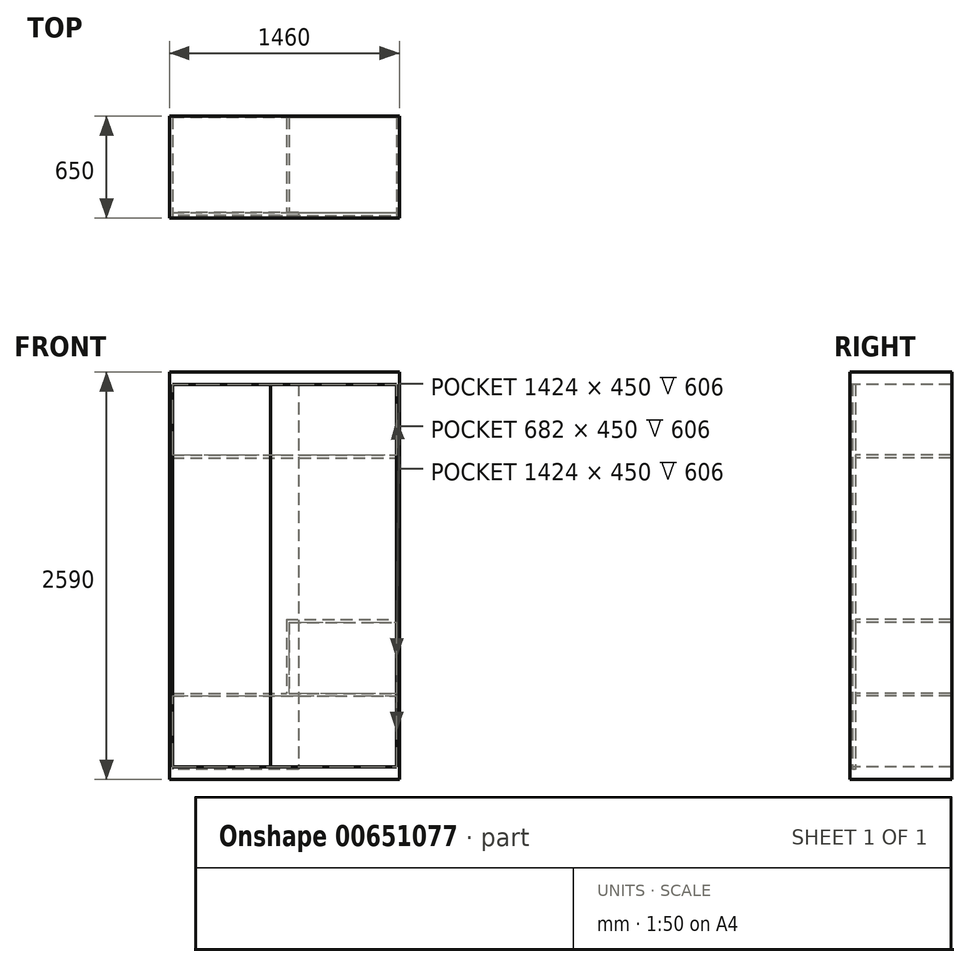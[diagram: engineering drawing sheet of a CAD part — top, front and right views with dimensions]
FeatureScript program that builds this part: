
annotation { "Feature Type Name" : "Feature", "Feature Type Description" : "" }
export const myFeature = defineFeature(function(context is Context, id is Id, definition is map)
    precondition{}
    {
        {
            var Q0;
            Q0=qCreatedBy(makeId("Top.planeOp"),FACE);
            var sketch = newSketch(context, id + "F0", { "sketchPlane" : qUnion([Q0])});
            skLineSegment(sketch, "E0.bottom", {"start": v(0, 0) * mm, "end": v(-1460, 0) * mm});
            skLineSegment(sketch, "E0.top", {"start": v(0, 650) * mm, "end": v(-1460, 650) * mm});
            skLineSegment(sketch, "E0.left", {"start": v(0, 0) * mm, "end": v(0, 650) * mm});
            skLineSegment(sketch, "E0.right", {"start": v(-1460, 0) * mm, "end": v(-1460, 650) * mm});
            skPoint(sketch, "E1.oppositeSnap0", {"position": v(-1460, 325) * mm});
            skLineSegment(sketch, "E1.bottom", {"start": v(-1460, 0) * mm, "end": v(-2355, 0) * mm});
            skLineSegment(sketch, "E1.left", {"start": v(-1460, 0) * mm, "end": v(-1460, 325) * mm});
            skLineSegment(sketch, "E1.right", {"start": v(-2355, 0) * mm, "end": v(-2355, 325) * mm});
            skLineSegment(sketch, "E2.bottom", {"start": v(-1460, 430) * mm, "end": v(-2355, 430) * mm});
            skLineSegment(sketch, "E2.left", {"start": v(-1460, 430) * mm, "end": v(-1460, 325) * mm});
            skLineSegment(sketch, "E2.right", {"start": v(-2355, 430) * mm, "end": v(-2355, 325) * mm});
            skSolve(sketch);
        }
        {
            var Q0;
            Q0=makeQuery(id+"F0.imprint","IMPRINT",FACE,{"disambiguationData":[TD([[makeQuery(id+"F0.imprint","IMPRINT",EDGE,{"derivedFrom":sQuery(id+"F0.wireOp",EDGE,"E0.bottom")}),-1.0]])]});
            extrude(context, id + "F1", {"entities" : qUnion([Q0]), "depth" : 2590 * mm, "offsetDistance" : 25 * mm});
        }
        {
            var Q0;
            Q0=makeQuery(id+"F1.opExtrude","SWEPT_FACE",FACE,{"disambiguationData":[OSD([sQuery(id+"F0.wireOp",EDGE,"E0.bottom")])]});
            var sketch = newSketch(context, id + "F2", { "sketchPlane" : qUnion([Q0])});
            skLineSegment(sketch, "E3.bottom", {"start": v(-1442, 2510) * mm, "end": v(-18, 2510) * mm});
            skLineSegment(sketch, "E3.top", {"start": v(-1442, 80) * mm, "end": v(-18, 80) * mm});
            skLineSegment(sketch, "E3.left", {"start": v(-1442, 2510) * mm, "end": v(-1442, 80) * mm});
            skLineSegment(sketch, "E3.right", {"start": v(-18, 2510) * mm, "end": v(-18, 80) * mm});
            skSolve(sketch);
        }
        {
            var Q0;
            Q0=qSketchRegion(id+"F2",true);
            extrude(context, id + "F3", {"entities" : qUnion([Q0]), "operationType" : NewBodyOperationType.REMOVE, "oppositeDirection" : true, "depth" : 36 * mm, "offsetDistance" : 25 * mm});
        }
        {
            var Q0;
            Q0=makeQuery(id+"F3.boolean.opBoolean","COPY",FACE,{"derivedFrom":makeQuery(id+"F3.opExtrude","CAP_FACE",FACE,{"disambiguationData":[OSD([sQuery(id+"F2.wireOp",EDGE,"E3.bottom"),sQuery(id+"F2.wireOp",EDGE,"E3.top"),sQuery(id+"F2.wireOp",EDGE,"E3.left"),sQuery(id+"F2.wireOp",EDGE,"E3.right")])],"isStart":false})});
            var sketch = newSketch(context, id + "F4", { "sketchPlane" : qUnion([Q0])});
            skLineSegment(sketch, "E4.bottom", {"start": v(-1442, 2510) * mm, "end": v(-18, 2510) * mm});
            skLineSegment(sketch, "E4.top", {"start": v(-1442, 2060) * mm, "end": v(-18, 2060) * mm});
            skLineSegment(sketch, "E4.left", {"start": v(-1442, 2510) * mm, "end": v(-1442, 2060) * mm});
            skLineSegment(sketch, "E4.right", {"start": v(-18, 2510) * mm, "end": v(-18, 2060) * mm});
            skLineSegment(sketch, "E5.bottom", {"start": v(-1442, 2042) * mm, "end": v(-18, 2042) * mm});
            skLineSegment(sketch, "E5.top", {"start": v(-718, 1016) * mm, "end": v(-18, 1016) * mm});
            skLineSegment(sketch, "E5.right", {"start": v(-18, 2042) * mm, "end": v(-18, 1016) * mm});
            skLineSegment(sketch, "E6.top", {"start": v(-1442, 548) * mm, "end": v(-718, 548) * mm});
            skLineSegment(sketch, "E6.right", {"start": v(-718, 1016) * mm, "end": v(-718, 548) * mm});
            skLineSegment(sketch, "E7.left", {"start": v(-1442, 530) * mm, "end": v(-1442, 104.26) * mm});
            skLineSegment(sketch, "E8.bottom", {"start": v(-700, 998) * mm, "end": v(-18, 998) * mm});
            skLineSegment(sketch, "E8.top", {"start": v(-700, 548) * mm, "end": v(-18, 548) * mm});
            skLineSegment(sketch, "E8.left", {"start": v(-700, 998) * mm, "end": v(-700, 548) * mm});
            skLineSegment(sketch, "E8.right", {"start": v(-18, 998) * mm, "end": v(-18, 548) * mm});
            skLineSegment(sketch, "E9.bottom", {"start": v(-1442, 530) * mm, "end": v(-18, 530) * mm});
            skLineSegment(sketch, "E9.right", {"start": v(-18, 530) * mm, "end": v(-18, 80) * mm});
            skSolve(sketch);
        }
        {
            var Q0;
            Q0=makeQuery(id+"F4.imprint","IMPRINT",FACE,{"disambiguationData":[TD([[makeQuery(id+"F4.imprint","IMPRINT",EDGE,{"derivedFrom":sQuery(id+"F4.wireOp",EDGE,"E4.bottom")}),-1.0]])]});
            var Q1;
            Q1=makeQuery(id+"F4.imprint","IMPRINT",FACE,{"disambiguationData":[TD([[makeQuery(id+"F4.imprint","IMPRINT",EDGE,{"derivedFrom":sQuery(id+"F4.wireOp",EDGE,"E8.bottom")}),-1.0]])]});
            var Q2;
            {var subQ1=sQuery(id+"F4.wireOp",EDGE,"E5.bottom");Q2=makeQuery(id+"F4.imprint","IMPRINT",FACE,{"disambiguationData":[TD([[makeQuery(id+"F4.imprint","IMPRINT",EDGE,{"derivedFrom":subQ1}),-1.0]])]});}
            var Q3;
            Q3=makeQuery(id+"F4.imprint","IMPRINT",FACE,{"disambiguationData":[TD([[makeQuery(id+"F4.imprint","IMPRINT",EDGE,{"derivedFrom":sQuery(id+"F4.wireOp",EDGE,"E9.bottom")}),-1.0]])]});
            extrude(context, id + "F5", {"entities" : qUnion([Q0, Q1, Q2, Q3]), "operationType" : NewBodyOperationType.REMOVE, "oppositeDirection" : true, "depth" : 606 * mm, "offsetDistance" : 25 * mm});
        }
        {
            var Q0;
            Q0=makeQuery(id+"F5.boolean.opBoolean","MERGE",FACE,{"derivedFrom":[makeQuery(id+"F3.boolean.opBoolean","COPY",FACE,{"derivedFrom":makeQuery(id+"F3.opExtrude","SWEPT_FACE",FACE,{"disambiguationData":[OSD([sQuery(id+"F2.wireOp",EDGE,"E3.right")])]})}),makeQuery(id+"F5.opExtrude","SWEPT_FACE",FACE,{"disambiguationData":[OSD([sQuery(id+"F4.wireOp",EDGE,"E4.right")])]}),makeQuery(id+"F5.opExtrude","SWEPT_FACE",FACE,{"disambiguationData":[OSD([sQuery(id+"F4.wireOp",EDGE,"E5.right")])]}),makeQuery(id+"F5.opExtrude","SWEPT_FACE",FACE,{"disambiguationData":[OSD([sQuery(id+"F4.wireOp",EDGE,"E8.right")])]}),makeQuery(id+"F5.opExtrude","SWEPT_FACE",FACE,{"disambiguationData":[OSD([sQuery(id+"F4.wireOp",EDGE,"E9.right")])]})]});
            var sketch = newSketch(context, id + "F6", { "sketchPlane" : qUnion([Q0])});
            skLineSegment(sketch, "E10.0", {"start": v(0, 2510) * mm, "end": v(0, 80) * mm});
            skLineSegment(sketch, "E11.bottom", {"start": v(0, 2510) * mm, "end": v(-18, 2510) * mm});
            skLineSegment(sketch, "E11.top", {"start": v(0, 80) * mm, "end": v(-18, 80) * mm});
            skLineSegment(sketch, "E11.right", {"start": v(-18, 2510) * mm, "end": v(-18, 80) * mm});
            skSolve(sketch);
        }
        {
            var Q0;
            Q0=qSketchRegion(id+"F6",true);
            extrude(context, id + "F7", {"entities" : qUnion([Q0]), "depth" : 800 * mm, "offsetDistance" : 25 * mm});
        }
        {
            var Q0;
            {var subQ0=sQuery(id+"F2.wireOp",EDGE,"E3.left");Q0=makeQuery(id+"F5.boolean.opBoolean","MERGE",FACE,{"derivedFrom":[makeQuery(id+"F3.boolean.opBoolean","COPY",FACE,{"derivedFrom":makeQuery(id+"F3.opExtrude","SWEPT_FACE",FACE,{"disambiguationData":[OSD([subQ0])]})}),makeQuery(id+"F5.opExtrude","SWEPT_FACE",FACE,{"disambiguationData":[OSD([sQuery(id+"F4.wireOp",EDGE,"E4.left")])]}),makeQuery(id+"F5.opExtrude","SWEPT_FACE",FACE,{"disambiguationData":[OSD([subQ0,sQuery(id+"F4.wireOp",EDGE,"E7.left")])]}),makeQuery(id+"F5.opExtrude","SWEPT_FACE",FACE,{"disambiguationData":[OSD([subQ0])]})]});}
            var sketch = newSketch(context, id + "F8", { "sketchPlane" : qUnion([Q0])});
            skLineSegment(sketch, "E12.bottom", {"start": v(36, 2510) * mm, "end": v(18, 2510) * mm});
            skLineSegment(sketch, "E12.top", {"start": v(36, 65.12) * mm, "end": v(18, 65.12) * mm});
            skLineSegment(sketch, "E12.left", {"start": v(36, 2510) * mm, "end": v(36, 65.12) * mm});
            skLineSegment(sketch, "E12.right", {"start": v(18, 2510) * mm, "end": v(18, 65.12) * mm});
            skSolve(sketch);
        }
        {
            var Q0;
            Q0=qSketchRegion(id+"F8",true);
            extrude(context, id + "F9", {"entities" : qUnion([Q0]), "depth" : 800 * mm, "offsetDistance" : 25 * mm});
        }
    });
